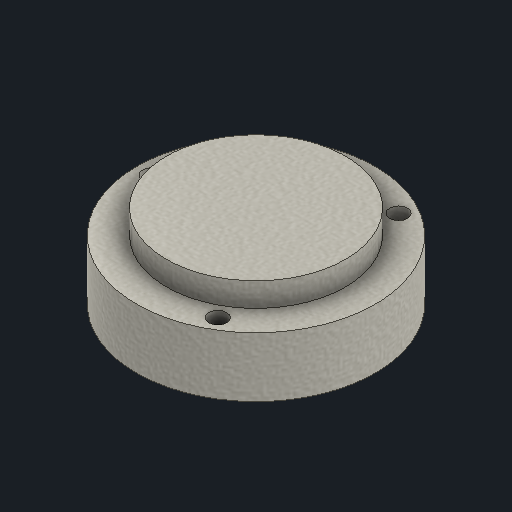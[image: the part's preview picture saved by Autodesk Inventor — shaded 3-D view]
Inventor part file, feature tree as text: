
AUTODESK INVENTOR PART (.ipt)
format: ipt  version: 2022 (Build 260153000, 153)  size: 224,768 bytes
history: native  units: mm
features: extrude x3, sketch x3, other x1
ambient origin geometry x8: Origin, YZ Plane, XZ Plane, XY Plane, X Axis, Y Axis, Z Axis, Center Point
bodies: Body1 (feature_tree)
feature tree (7):
  other  "Sólido1"
  extrude  "Extrusión1"  Depth=40.0mm
  extrude  "Extrusión2"  Depth=3.0mm
  extrude  "Extrusión3"  TaperAngle=120.0deg  [1 undecoded]
  sketch  "Boceto1"  dims[d4=25.0mm d5=40.0mm]
  sketch  "Boceto2"  dims[d6=3.0mm d7=3.0mm]
  sketch  "Boceto3"  dims[d8=3.0mm d10=120.0deg d11=120.0deg d12=17.5mm d13=17.5mm d14=17.5mm d15=10.0mm d16=0.0mm d17=30.0mm d18=2.5mm d19=0.0mm d20=1.5mm d21=0.0mm]
note: 1 required parameter value undecoded (feature->parameter linkage not recoverable at this tier; creation-order binding heuristic only, values carry confidence <= 0.55)
